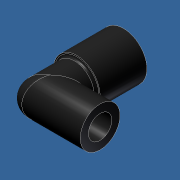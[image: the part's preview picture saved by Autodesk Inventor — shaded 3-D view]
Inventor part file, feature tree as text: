
AUTODESK INVENTOR PART (.ipt)
format: ipt  version: unknown  size: 256,512 bytes
history: native  units: in
note: dims shown in document units (in); Inventor stores cm internally (conversion verified against a paired STEP export)
features: extrude x5, sketch x4, plane x2, fillet x2, projected_geometry x1
ambient origin geometry x8: Origin, YZ Plane, XZ Plane, XY Plane, X Axis, Y Axis, Z Axis, Center Point
bodies: Solid1 (feature_tree)
feature tree (14):
  extrude  "Extrusion1"  Depth=0.5in
  extrude  "Extrusion2"  Depth=0.425in
  plane  "Work Plane1"
  sketch  "Sketch3"  dims[d5=0.5in d6=0.0in d7=-0.83in]
  extrude  "Extrusion3"  [1 undecoded]
  extrude  "Extrusion4"  Depth=0.25in
  plane  "Work Plane2"
  extrude  "Extrusion5"  Depth=0.75in TaperAngle=0.0deg
  fillet  "Fillet1"  Radius=1.0in
  fillet  "Fillet2"  Radius=0.5in
  sketch  "Sketch1"  dims[d0=0.25in d1=0.5in]
  sketch  "Sketch2"  dims[d2=0.5in d3=0.0in d4=0.425in]
  projected_geometry  "Projected Loop1"
  sketch  "Sketch4"  dims[d8=0.75in d9=0.0in d10=0.25in d11=0.75in d12=0.0in d13=1.0in d14=0.5in d15=0.0in d16=0.125in d17=0.025in]
note: 1 required parameter value undecoded (feature->parameter linkage not recoverable at this tier; creation-order binding heuristic only, values carry confidence <= 0.55)
